# Revit family: Haworth_Epure_CompactDesk_Asymmetrical90_EU_PRELIMINARY
name_source: partatom
category: Furniture
units: mm (PartAtom-declared; Revit-internal decimal feet)

## family parameters
Always vertical = Yes
Cut with Voids When Loaded = No
OmniClass Number = 23.40.70.14.64.11
OmniClass Title = Office Furniture
Room Calculation Point = No
Shared = No
Work Plane-Based = No

## types (11) — shared parameters
Actual Height = 73 cm
Assembly Code = E2020200
Cable Outlet Graphics = Not available for Scallop and Actual Width > 190cm
Description = Haworth - Epure - Asymmetrical Compact Desk
Flip Top Finish = Haworth _ Paint _ Metallic Silver
Leg Depth = 40 cm
Leg Height = 70 cm
Manufacturer = Haworth
Model = EUCOLSXXXX
Revision Number = 1
Size = Verify Final Dim.w/ Haworth
Trim Finish = Haworth _ Metal _ Structured White EC
URL = https://www.haworth.com
URL - Product = https://www.haworth.com
Warranty = http://www.haworth.com

## per-type parameters (varying)
| type | Accessory Kit | Actual Depth | Actual Width | Cable Outlet | Flip Top Cable Outlet | Large | Leg Width | No Accessory Kit | Round Cable Outlet | Rounded Corners | Scallop | Small | Squared Corners |
| 200 x 120 - squared | Yes | 120 cm | 200 cm | No | Yes | Yes | 60 cm | No | No | No | No | No | Yes |
| 200 x 110 - squared | Yes | 110 cm | 200 cm | No | No | Yes | 60 cm | No | Yes | No | Yes | No | Yes |
| 180 x 120 - scallop | No | 120 cm | 180 cm | No | No | Yes | 60 cm | Yes | No | No | Yes | No | No |
| 160 x 120 - scallop - large | No | 120 cm | 160 cm | No | No | No | 40 cm | Yes | No | No | Yes | Yes | No |
| 160 x 120 - rounded - small | Yes | 120 cm | 160 cm | Yes | No | No | 40 cm | No | Yes | Yes | No | Yes | No |
| 180 x 120 - squared | No | 120 cm | 180 cm | No | No | Yes | 60 cm | Yes | No | No | No | No | Yes |
| 160 x 120 - rounded - large | Yes | 120 cm | 160 cm | Yes | Yes | No | 40 cm | No | No | Yes | No | Yes | No |
| 160 x 120 - squared - large | Yes | 120 cm | 160 cm | Yes | No | No | 40 cm | No | Yes | No | No | Yes | Yes |
| 160 x 120 - squared - small | Yes | 120 cm | 160 cm | Yes | No | No | 40 cm | No | No | No | No | Yes | Yes |
| 200 x 120 - scallop | Yes | 120 cm | 200 cm | No | Yes | Yes | 60 cm | No | No | No | Yes | No | No |
| 200 x 120 - rounded | Yes | 120 cm | 200 cm | No | Yes | Yes | 60 cm | No | No | Yes | No | No | No |

type visibility flags: 11 boolean params named "<type name>" — each type sets only its own to Yes (folded from table)

## geometry (parser evidence)
native form markers: Sweep x15
no freeform markers — native parametric forms only
